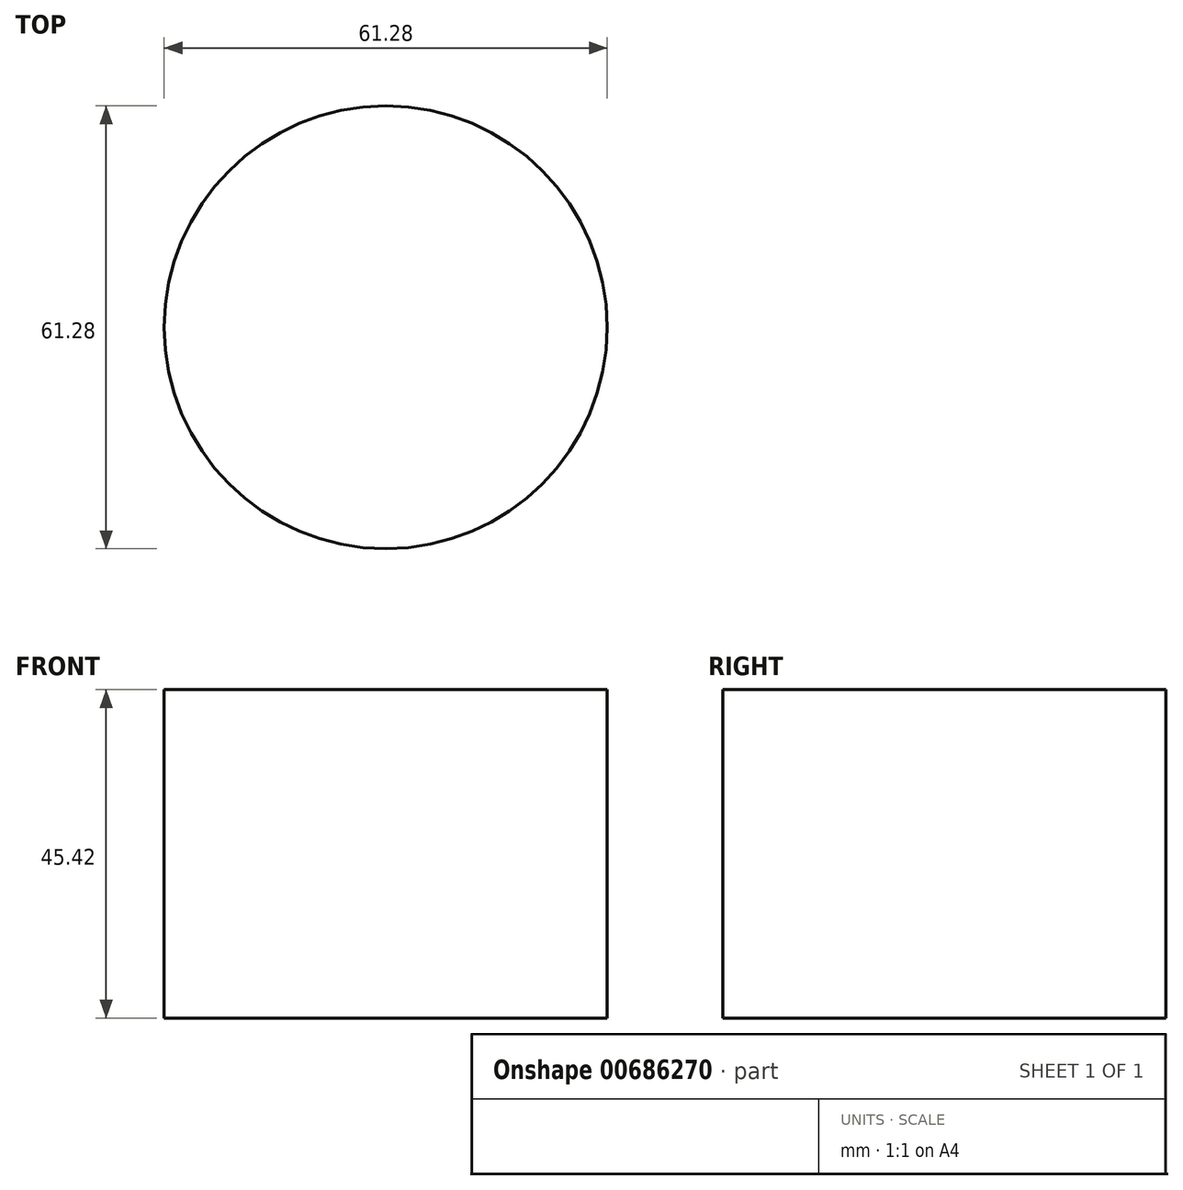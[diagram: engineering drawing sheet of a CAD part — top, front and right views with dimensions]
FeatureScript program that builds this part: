
annotation { "Feature Type Name" : "Feature", "Feature Type Description" : "" }
export const myFeature = defineFeature(function(context is Context, id is Id, definition is map)
    precondition{}
    {
        {
            var Q0;
            Q0=qCreatedBy(makeId("Right.planeOp"),FACE);
            var sketch = newSketch(context, id + "F0", { "sketchPlane" : qUnion([Q0])});
            skLineSegment(sketch, "E0.bottom", {"start": v(0, 0) * mm, "end": v(-30.64, 0) * mm});
            skLineSegment(sketch, "E0.top", {"start": v(0, 45.42) * mm, "end": v(-30.64, 45.42) * mm});
            skLineSegment(sketch, "E0.left", {"start": v(0, 0) * mm, "end": v(0, 45.42) * mm});
            skLineSegment(sketch, "E0.right", {"start": v(-30.64, 0) * mm, "end": v(-30.64, 45.42) * mm});
            skSolve(sketch);
        }
        {
            var Q0;
            Q0=makeQuery(id+"F0.imprint","IMPRINT",FACE,{"disambiguationData":[TD([[makeQuery(id+"F0.imprint","IMPRINT",EDGE,{"derivedFrom":sQuery(id+"F0.wireOp",EDGE,"E0.bottom")}),-1.0]])]});
            var Q1;
            Q1=sQuery(id+"F0.wireOp",EDGE,"E0.left");
            revolve(context, id + "F1", {"entities" : qUnion([Q0]), "axis" : qUnion([Q1]), "revolveType" : RevolveType.FULL});
        }
    });
